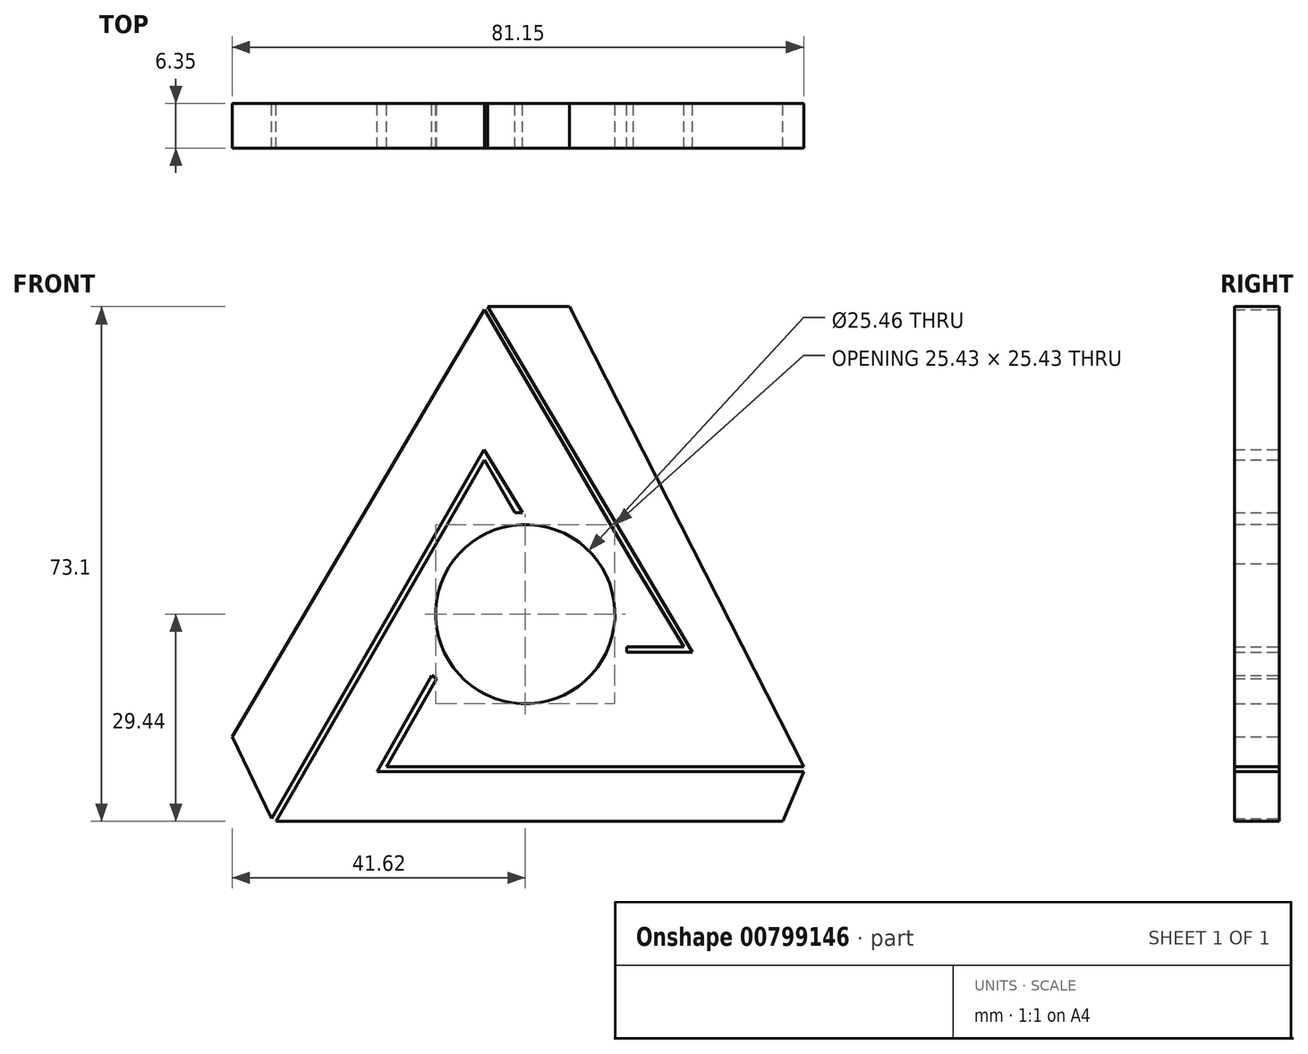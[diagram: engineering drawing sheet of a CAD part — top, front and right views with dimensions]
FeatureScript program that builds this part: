
annotation { "Feature Type Name" : "Feature", "Feature Type Description" : "" }
export const myFeature = defineFeature(function(context is Context, id is Id, definition is map)
    precondition{}
    {
        {
            var Q0;
            Q0=qCreatedBy(makeId("Front.planeOp"),FACE);
            var sketch = newSketch(context, id + "F0", { "sketchPlane" : qUnion([Q0])});
            skCircle(sketch, "E0", {"center": v(0, 0) * mm, "radius": 12.7 * mm});
            skLineSegment(sketch, "E1", {"start": v(11.81, -4.67) * mm, "end": v(22.5, -4.67) * mm});
            skLineSegment(sketch, "E2", {"start": v(22.5, -4.67) * mm, "end": v(15.33, 7.17) * mm});
            skLineSegment(sketch, "E3", {"start": v(15.33, 7.17) * mm, "end": v(8.83, 18.3) * mm});
            skLineSegment(sketch, "E4", {"start": v(8.83, 18.3) * mm, "end": v(5.1, 24.7) * mm});
            skLineSegment(sketch, "E5", {"start": v(5.1, 24.7) * mm, "end": v(2.52, 29.07) * mm});
            skLineSegment(sketch, "E6", {"start": v(2.52, 29.07) * mm, "end": v(-1.21, 35.4) * mm});
            skLineSegment(sketch, "E7", {"start": v(-1.21, 35.4) * mm, "end": v(-5.78, 43.25) * mm});
            skLineSegment(sketch, "E8", {"start": v(-5.78, 43.25) * mm, "end": v(-11.87, 33.03) * mm});
            skLineSegment(sketch, "E9", {"start": v(-11.87, 33.03) * mm, "end": v(-21.64, 16.47) * mm});
            skLineSegment(sketch, "E10", {"start": v(-21.64, 16.47) * mm, "end": v(-28.84, 4.26) * mm});
            skLineSegment(sketch, "E11", {"start": v(-28.84, 4.26) * mm, "end": v(-37.36, -10.18) * mm});
            skLineSegment(sketch, "E12", {"start": v(-37.36, -10.18) * mm, "end": v(-41.62, -17.4) * mm});
            skLineSegment(sketch, "E13", {"start": v(-41.62, -17.4) * mm, "end": v(-36, -29.02) * mm});
            skLineSegment(sketch, "E14", {"start": v(-36, -29.02) * mm, "end": v(-5.87, 23.38) * mm});
            skLineSegment(sketch, "E15", {"start": v(-5.87, 23.38) * mm, "end": v(0.66, 12.68) * mm});
            skLineSegment(sketch, "E16", {"start": v(-11.43, -5.53) * mm, "end": v(-21.03, -22.34) * mm});
            skLineSegment(sketch, "E17", {"start": v(-21.03, -22.34) * mm, "end": v(39.53, -22.34) * mm});
            skLineSegment(sketch, "E18", {"start": v(39.53, -22.34) * mm, "end": v(36.53, -29.44) * mm});
            skLineSegment(sketch, "E19", {"start": v(36.53, -29.44) * mm, "end": v(-35.37, -29.44) * mm});
            skLineSegment(sketch, "E20", {"start": v(-35.37, -29.44) * mm, "end": v(-5.82, 21.92) * mm});
            skLineSegment(sketch, "E21", {"start": v(-5.82, 21.92) * mm, "end": v(-0.44, 12.7) * mm});
            skLineSegment(sketch, "E22", {"start": v(39.53, -21.66) * mm, "end": v(-19.7, -21.66) * mm});
            skLineSegment(sketch, "E23", {"start": v(-19.7, -21.66) * mm, "end": v(-10.98, -6.38) * mm});
            skLineSegment(sketch, "E24", {"start": v(39.53, -21.66) * mm, "end": v(6.27, 43.66) * mm});
            skLineSegment(sketch, "E25", {"start": v(6.27, 43.66) * mm, "end": v(-5.33, 43.66) * mm});
            skLineSegment(sketch, "E26", {"start": v(-5.33, 43.66) * mm, "end": v(23.71, -5.42) * mm});
            skLineSegment(sketch, "E27", {"start": v(23.71, -5.42) * mm, "end": v(11.48, -5.42) * mm});
            skCircle(sketch, "E28", {"center": v(0, 0) * mm, "radius": 12.73 * mm});
            skLineSegment(sketch, "E29", {"start": v(-10.98, -6.38) * mm, "end": v(-12.56, -9.14) * mm});
            skLineSegment(sketch, "E30", {"start": v(-12.56, -9.14) * mm, "end": v(-13.26, -8.73) * mm});
            skLineSegment(sketch, "E31", {"start": v(-13.26, -8.73) * mm, "end": v(-11.43, -5.53) * mm});
            skLineSegment(sketch, "E32", {"start": v(-13.26, -8.73) * mm, "end": v(-12.56, -9.14) * mm});
            skLineSegment(sketch, "E33", {"start": v(11.81, -4.67) * mm, "end": v(14.4, -4.67) * mm});
            skLineSegment(sketch, "E34", {"start": v(14.4, -5.42) * mm, "end": v(11.48, -5.42) * mm});
            skLineSegment(sketch, "E35", {"start": v(14.4, -5.42) * mm, "end": v(14.4, -4.67) * mm});
            skLineSegment(sketch, "E36", {"start": v(-0.44, 12.7) * mm, "end": v(-1.45, 14.43) * mm});
            skLineSegment(sketch, "E37", {"start": v(0.64, 12.71) * mm, "end": v(0.66, 12.68) * mm});
            skPoint(sketch, "E38.end.orphan", {"position": v(-0.44, 14.43) * mm});
            skLineSegment(sketch, "E39", {"start": v(-1.45, 14.43) * mm, "end": v(-0.4, 14.43) * mm});
            skLineSegment(sketch, "E40", {"start": v(-0.4, 14.43) * mm, "end": v(0.64, 12.71) * mm});
            skSolve(sketch);
        }
        {
            var Q0;
            Q0=qSketchRegion(id+"F0",true);
            extrude(context, id + "F1", {"entities" : qUnion([Q0]), "depth" : 6.35 * mm, "offsetDistance" : 25.4 * mm});
        }
    });
